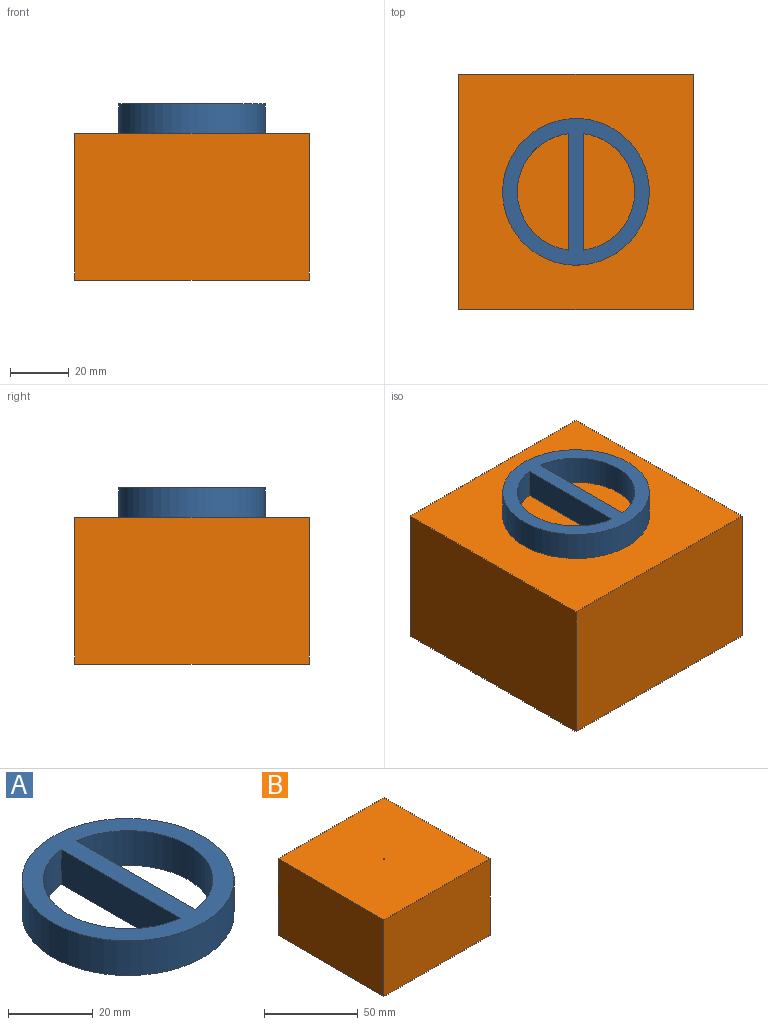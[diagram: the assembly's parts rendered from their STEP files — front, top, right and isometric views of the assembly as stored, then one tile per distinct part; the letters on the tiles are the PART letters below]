
ASSEMBLY  parts=2 mates=1
PART A: 7 faces, bbox 50x50x10 mm
  f0: cylinder r=25mm len=50mm, axis (0,0,-1), area 1570.8mm2, adj f1,f2
  f1: plane 50x50mm, normal (0,0,1), area 906.3mm2, adj f0,f3,f4,f5,f6
  f2: plane 50x50mm, normal (0,0,-1), area 906.3mm2, adj f0,f3,f4,f5,f6
  f3: plane 39.69x10mm, normal (1,0,0), area 396.9mm2, adj f1,f2,f4
  f4: cylinder r=20mm len=39.69mm, axis (0,0,1), area 578.2mm2, adj f1,f2,f3
  f5: plane 39.69x10mm, normal (-1,0,0), area 396.9mm2, adj f1,f2,f6
  f6: cylinder r=20mm len=39.69mm, axis (0,0,1), area 578.2mm2, adj f1,f2,f5
PART B: 8 faces, bbox 80x80x50 mm
  f0: plane 80x50mm, normal (-1,0,0), area 4000mm2, adj f1,f3,f4,f5
  f1: plane 80x50mm, normal (0,-1,0), area 4000mm2, adj f0,f2,f4,f5
  f2: plane 80x50mm, normal (1,0,0), area 4000mm2, adj f1,f3,f4,f5
  f3: plane 80x50mm, normal (0,1,0), area 4000mm2, adj f0,f2,f4,f5
  f4: plane 80x80mm, normal (0,0,1), area 6399.2mm2, adj f0,f1,f2,f3,f6
  f5: plane 80x80mm, normal (0,0,-1), area 6400mm2, adj f0,f1,f2,f3
  f6: cylinder r=0.5mm len=1mm, axis (0,0,1), area 3.1mm2, adj f4,f7
  f7: plane 1x1mm, normal (0,0,1), area 0.8mm2, adj f6
PLACE A t=(-19.48,-21.06,11.28)mm
PLACE B t=(-59.48,18.94,-38.72)mm
MATE revolute A.f0 <-> B.f6  axis (0,0,-1) through (-19.48,-21.06,11.28)mm
